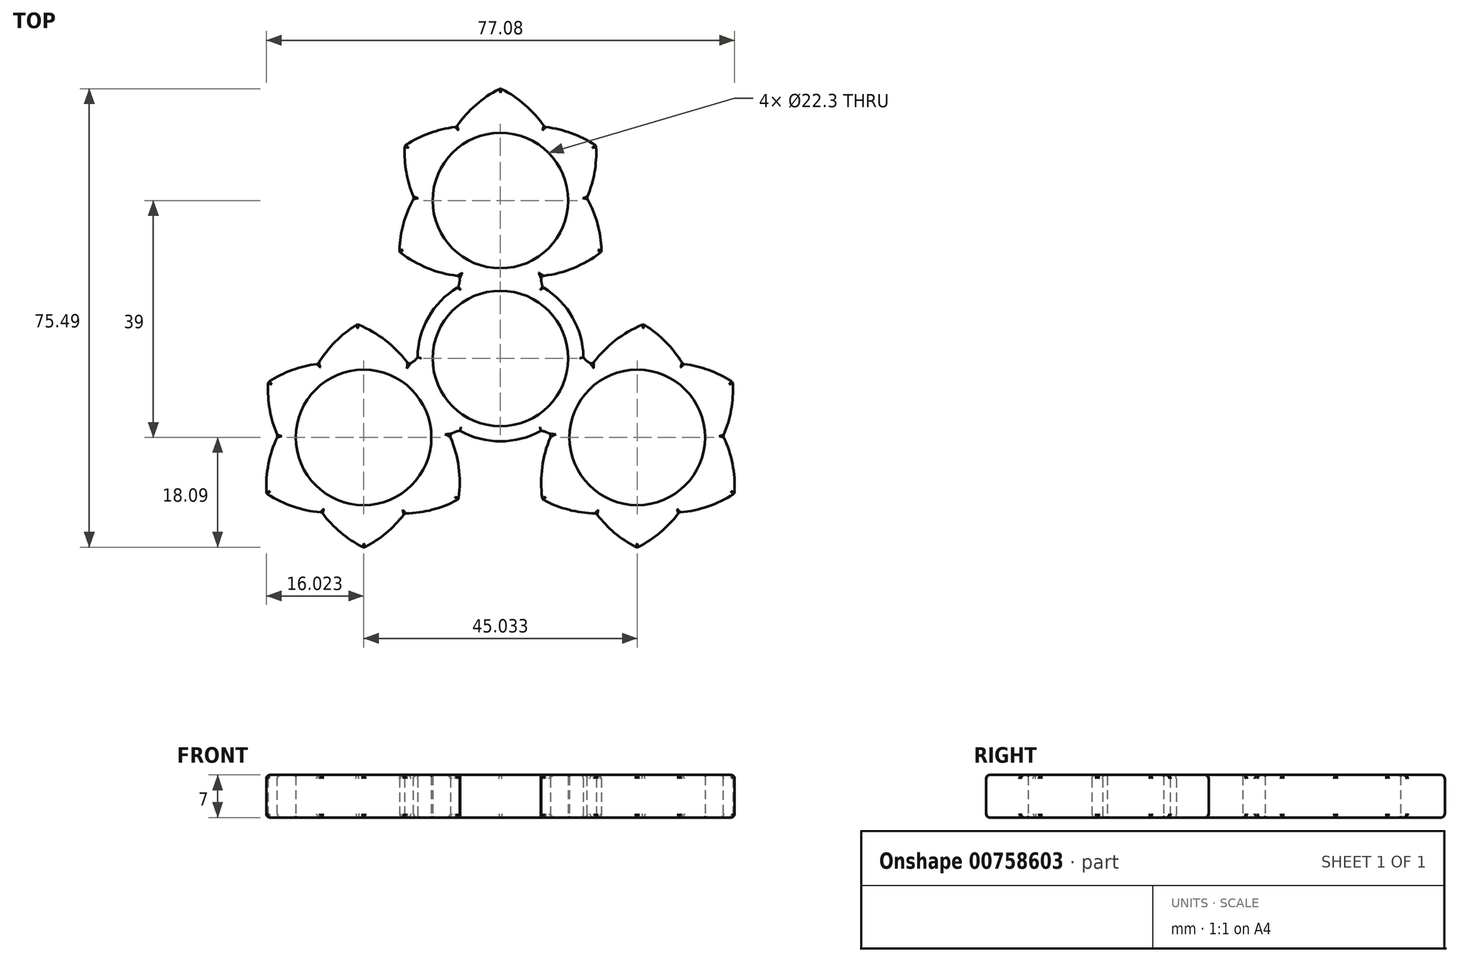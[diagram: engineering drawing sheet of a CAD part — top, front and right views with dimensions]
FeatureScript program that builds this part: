
annotation { "Feature Type Name" : "Feature", "Feature Type Description" : "" }
export const myFeature = defineFeature(function(context is Context, id is Id, definition is map)
    precondition{}
    {
        {
            var Q0;
            Q0=qCreatedBy(makeId("Top.planeOp"),FACE);
            var sketch = newSketch(context, id + "F0", { "sketchPlane" : qUnion([Q0])});
            skCircle(sketch, "E0", {"center": v(0, 0) * mm, "radius": 11.15 * mm});
            skArc(sketch, "E1.0", {"start": v(-5.17, 12.63) * mm, "mid": v(-6.92, 11.76) * mm, "end": v(-8.53, 10.66) * mm, "construction": true});
            skLineSegment(sketch, "E2", {"start": v(0, 0) * mm, "end": v(0, 26) * mm, "construction": true});
            skCircle(sketch, "E3", {"center": v(0, 26) * mm, "radius": 11.15 * mm});
            skArc(sketch, "E4.0", {"start": v(7, 14.28) * mm, "mid": v(0, 39.65) * mm, "end": v(-7, 14.28) * mm});
            skPoint(sketch, "E5.visualSharp", {"position": v(0, 16.7) * mm});
            skLineSegment(sketch, "E6.0", {"start": v(7, 0) * mm, "end": v(7, 29.5) * mm, "construction": true});
            skArc(sketch, "E7.trimOffspring", {"start": v(-7, 11.72) * mm, "mid": v(0, -13.65) * mm, "end": v(7, 11.72) * mm});
            skArc(sketch, "E8", {"start": v(7, 14.28) * mm, "mid": v(6.7, 13) * mm, "end": v(7, 11.72) * mm});
            skArc(sketch, "E9.MirrorCS", {"start": v(-7, 14.28) * mm, "mid": v(-6.7, 13) * mm, "end": v(-7, 11.72) * mm});
            skArc(sketch, "E10", {"start": v(0, 44.46) * mm, "mid": v(-4.47, 41.37) * mm, "end": v(-7.9, 37.13) * mm});
            skArc(sketch, "E11.MirrorCS", {"start": v(0, 44.46) * mm, "mid": v(4.47, 41.37) * mm, "end": v(7.9, 37.13) * mm});
            skArc(sketch, "E12", {"start": v(16.64, 17.58) * mm, "mid": v(15.74, 22.94) * mm, "end": v(13.37, 27.84) * mm});
            skArc(sketch, "E13.MirrorCS", {"start": v(16.64, 17.58) * mm, "mid": v(11.93, 14.85) * mm, "end": v(6.64, 13.55) * mm});
            skArc(sketch, "E14.MirrorCS", {"start": v(-15.74, 35.04) * mm, "mid": v(-15.27, 29.62) * mm, "end": v(-13.3, 24.55) * mm});
            skArc(sketch, "E15.MirrorCS", {"start": v(-15.74, 35.04) * mm, "mid": v(-10.82, 37.39) * mm, "end": v(-5.45, 38.25) * mm});
            skArc(sketch, "E16.MirrorCS", {"start": v(15.74, 35.04) * mm, "mid": v(10.82, 37.39) * mm, "end": v(5.45, 38.25) * mm});
            skArc(sketch, "E17.MirrorCS", {"start": v(15.74, 35.04) * mm, "mid": v(15.27, 29.62) * mm, "end": v(13.3, 24.55) * mm});
            skArc(sketch, "E18.MirrorCS", {"start": v(-16.64, 17.58) * mm, "mid": v(-15.74, 22.94) * mm, "end": v(-13.37, 27.84) * mm});
            skArc(sketch, "E19.MirrorCS", {"start": v(-16.64, 17.58) * mm, "mid": v(-11.93, 14.85) * mm, "end": v(-6.64, 13.55) * mm});
            skSolve(sketch);
        }
        {
            var Q0;
            Q0=qSketchRegion(id+"F2",true);
            var Q1;
            Q1=qSketchRegion(id+"F0",true);
            var Q2;
            {var subQ0=sQuery(id+"F0.wireOp",EDGE,"5286eaf0-ed28-4451-94e3-1d908ec19ca7");var subQ1=sQuery(id+"F0.wireOp",EDGE,"E3");var subQ2=makeQuery(id+"F0.imprint","INTERSECT",VERTEX,{"disambiguationData":[OD(0.0)],"derivedFrom":[subQ1,subQ0]});Q2=makeQuery(id+"F0.imprint","IMPRINT",FACE,{"disambiguationData":[TD([[makeQuery(id+"F0.imprint","IMPRINT",EDGE,{"disambiguationData":[TD([[subQ2,-1.0]])],"derivedFrom":subQ1}),-1.0]])]});}
            var Q3;
            {var subQ0=sQuery(id+"F0.wireOp",EDGE,"972e2314-292c-46cc-950a-d2e98ffed2b1");var subQ1=sQuery(id+"F0.wireOp",EDGE,"E3");var subQ2=makeQuery(id+"F0.imprint","INTERSECT",VERTEX,{"disambiguationData":[OD(0.0)],"derivedFrom":[subQ1,subQ0]});Q3=makeQuery(id+"F0.imprint","IMPRINT",FACE,{"disambiguationData":[TD([[makeQuery(id+"F0.imprint","IMPRINT",EDGE,{"disambiguationData":[TD([[subQ2,-1.0]])],"derivedFrom":subQ1}),-1.0]])]});}
            var Q4;
            {var subQ0=sQuery(id+"F0.wireOp",EDGE,"8576df35-fd95-4b7d-8476-f7b5d8a5ebd1");var subQ1=sQuery(id+"F0.wireOp",EDGE,"E3");var subQ2=makeQuery(id+"F0.imprint","INTERSECT",VERTEX,{"disambiguationData":[OD(0.0)],"derivedFrom":[subQ1,subQ0]});Q4=makeQuery(id+"F0.imprint","IMPRINT",FACE,{"disambiguationData":[TD([[makeQuery(id+"F0.imprint","IMPRINT",EDGE,{"disambiguationData":[TD([[subQ2,-1.0]])],"derivedFrom":subQ1}),-1.0]])]});}
            var Q5;
            {var subQ0=sQuery(id+"F0.wireOp",EDGE,"upsWoKqN-qIG4-cDSa-tKJD-hM69GbnP515O");var subQ1=sQuery(id+"F0.wireOp",EDGE,"E3");var subQ2=makeQuery(id+"F0.imprint","INTERSECT",VERTEX,{"disambiguationData":[OD(0.0)],"derivedFrom":[subQ1,subQ0]});Q5=makeQuery(id+"F0.imprint","IMPRINT",FACE,{"disambiguationData":[TD([[makeQuery(id+"F0.imprint","IMPRINT",EDGE,{"disambiguationData":[TD([[subQ2,-1.0]])],"derivedFrom":subQ1}),-1.0]])]});}
            var Q6;
            {var subQ0=sQuery(id+"F0.wireOp",EDGE,"2dc68220-ebba-422f-adc0-bbb553f4a656");var subQ1=sQuery(id+"F0.wireOp",EDGE,"E3");var subQ2=makeQuery(id+"F0.imprint","INTERSECT",VERTEX,{"disambiguationData":[OD(0.0)],"derivedFrom":[subQ1,subQ0]});Q6=makeQuery(id+"F0.imprint","IMPRINT",FACE,{"disambiguationData":[TD([[makeQuery(id+"F0.imprint","IMPRINT",EDGE,{"disambiguationData":[TD([[subQ2,-1.0]])],"derivedFrom":subQ1}),-1.0]])]});}
            var Q7;
            {var subQ0=sQuery(id+"F0.wireOp",EDGE,"70cbc2a9-83ff-4b48-bb73-ff75b1e053e5");var subQ1=sQuery(id+"F0.wireOp",EDGE,"E3");var subQ2=makeQuery(id+"F0.imprint","INTERSECT",VERTEX,{"disambiguationData":[OD(0.0)],"derivedFrom":[subQ1,subQ0]});Q7=makeQuery(id+"F0.imprint","IMPRINT",FACE,{"disambiguationData":[TD([[makeQuery(id+"F0.imprint","IMPRINT",EDGE,{"disambiguationData":[TD([[subQ2,1.0]])],"derivedFrom":subQ1}),-1.0]])]});}
            var Q8;
            {var subQ0=sQuery(id+"F0.wireOp",EDGE,"8457dc48-e8ce-439c-b6e1-438fe0c9034f");var subQ1=sQuery(id+"F0.wireOp",EDGE,"E3");var subQ2=makeQuery(id+"F0.imprint","INTERSECT",VERTEX,{"disambiguationData":[OD(0.0)],"derivedFrom":[subQ1,subQ0]});Q8=makeQuery(id+"F0.imprint","IMPRINT",FACE,{"disambiguationData":[TD([[makeQuery(id+"F0.imprint","IMPRINT",EDGE,{"disambiguationData":[TD([[subQ2,-1.0]])],"derivedFrom":subQ1}),-1.0]])]});}
            var Q9;
            {var subQ0=sQuery(id+"F0.wireOp",EDGE,"6db5ce6a-88a4-4cba-8603-f791245f7d5f");var subQ1=sQuery(id+"F0.wireOp",EDGE,"E3");var subQ2=makeQuery(id+"F0.imprint","INTERSECT",VERTEX,{"disambiguationData":[OD(0.0)],"derivedFrom":[subQ1,subQ0]});Q9=makeQuery(id+"F0.imprint","IMPRINT",FACE,{"disambiguationData":[TD([[makeQuery(id+"F0.imprint","IMPRINT",EDGE,{"disambiguationData":[TD([[subQ2,-1.0]])],"derivedFrom":subQ1}),-1.0]])]});}
            var Q10;
            {var subQ0=sQuery(id+"F0.wireOp",EDGE,"26ba9915-316d-43ac-97a0-efcd31670470");var subQ1=sQuery(id+"F0.wireOp",EDGE,"E3");var subQ2=makeQuery(id+"F0.imprint","INTERSECT",VERTEX,{"disambiguationData":[OD(0.0)],"derivedFrom":[subQ1,subQ0]});Q10=makeQuery(id+"F0.imprint","IMPRINT",FACE,{"disambiguationData":[TD([[makeQuery(id+"F0.imprint","IMPRINT",EDGE,{"disambiguationData":[TD([[subQ2,-1.0]])],"derivedFrom":subQ1}),-1.0]])]});}
            extrude(context, id + "F1", {"entities" : qUnion([Q0, Q1, Q2, Q3, Q4, Q5, Q6, Q7, Q8, Q9, Q10]), "depth" : 7 * mm, "offsetDistance" : 25 * mm});
        }
        {
            var Q0;
            Q0=qCreatedBy(makeId("Right.planeOp"),FACE);
            var sketch = newSketch(context, id + "F2", { "sketchPlane" : qUnion([Q0])});
            skLineSegment(sketch, "E20", {"start": v(0, -11.35) * mm, "end": v(0, 14.45) * mm, "construction": true});
            skSolve(sketch);
        }
        {
            var Q0;
            Q0=makeQuery(id+"F1.opExtrude","SWEPT_FACE",FACE,{"disambiguationData":[OSD([sQuery(id+"F0.wireOp",EDGE,"E0")])]});
            var Q1;
            Q1=makeQuery(id+"F1.opExtrude","SWEPT_FACE",FACE,{"disambiguationData":[OSD([sQuery(id+"F0.wireOp",EDGE,"E3")])]});
            fillet(context, id + "F3", {"entities" : qUnion([Q0, Q1]), "radius" : 0.2 * mm, "tangentPropagation" : true, "allowEdgeOverflow" : false});
        }
        {
            var Q0;
            Q0=makeQuery(id+"F1.opExtrude","SWEPT_EDGE",EDGE,{"disambiguationData":[OSD([sQuery(id+"F0.wireOp",EDGE,"B6IW4b8f-rdPB-c0Us-c8Mo-Mq4TzhgtsJ4K"),sQuery(id+"F0.wireOp",EDGE,"YkMFX2vO-4Crt-TsgE-euFS-UGkuE4yFQV92")])]});
            var Q1;
            Q1=makeQuery(id+"F1.opExtrude","SWEPT_EDGE",EDGE,{"disambiguationData":[OSD([sQuery(id+"F0.wireOp",EDGE,"05Ssocvi-DhHh-OsZG-e2E6-rp3hOyrowWxE"),sQuery(id+"F0.wireOp",EDGE,"gXTc2K6m-pDrj-VkwX-DA3g-2FsoQV2dXgWA")])]});
            var Q2;
            Q2=makeQuery(id+"F1.opExtrude","SWEPT_EDGE",EDGE,{"disambiguationData":[OSD([sQuery(id+"F0.wireOp",EDGE,"WV1YJwpc-lhCt-Tkbw-pyGD-IAguLvoMxcio"),sQuery(id+"F0.wireOp",EDGE,"lRAOphcG-mkQV-B9rX-murS-RDVpryX3sv7Y")])]});
            var Q3;
            Q3=makeQuery(id+"F1.opExtrude","CAP_FACE",FACE,{"disambiguationData":[OSD([sQuery(id+"F0.wireOp",EDGE,"E0"),sQuery(id+"F0.wireOp",EDGE,"E3"),sQuery(id+"F0.wireOp",EDGE,"E4.0"),sQuery(id+"F0.wireOp",EDGE,"E7.trimOffspring"),sQuery(id+"F0.wireOp",EDGE,"E8"),sQuery(id+"F0.wireOp",EDGE,"E9.MirrorCS"),sQuery(id+"F0.wireOp",EDGE,"A4q6XAE9-nX4I-gney-ZS84-N0PxHdFMNtC2"),sQuery(id+"F0.wireOp",EDGE,"90f88150-1d21-4d5f-99c7-c443b2953583"),sQuery(id+"F0.wireOp",EDGE,"aea63897-bdd4-478d-acf8-b9e86850efd0"),sQuery(id+"F0.wireOp",EDGE,"e52c3788-5800-4ccf-9de2-e600990ce032"),sQuery(id+"F0.wireOp",EDGE,"6943e6b1-6e27-4218-960a-470c6ffbd814"),sQuery(id+"F0.wireOp",EDGE,"dd87b57e-f014-4439-b0ae-6b8a5318a583"),sQuery(id+"F0.wireOp",EDGE,"9d18db76-b666-4d6e-9b71-35c6185a29a1")])],"isStart":false});
            var Q4;
            Q4=makeQuery(id+"F1.opExtrude","CAP_FACE",FACE,{"disambiguationData":[OSD([sQuery(id+"F0.wireOp",EDGE,"E0"),sQuery(id+"F0.wireOp",EDGE,"E3"),sQuery(id+"F0.wireOp",EDGE,"E4.0"),sQuery(id+"F0.wireOp",EDGE,"E7.trimOffspring"),sQuery(id+"F0.wireOp",EDGE,"E8"),sQuery(id+"F0.wireOp",EDGE,"E9.MirrorCS"),sQuery(id+"F0.wireOp",EDGE,"A4q6XAE9-nX4I-gney-ZS84-N0PxHdFMNtC2"),sQuery(id+"F0.wireOp",EDGE,"90f88150-1d21-4d5f-99c7-c443b2953583"),sQuery(id+"F0.wireOp",EDGE,"aea63897-bdd4-478d-acf8-b9e86850efd0"),sQuery(id+"F0.wireOp",EDGE,"e52c3788-5800-4ccf-9de2-e600990ce032"),sQuery(id+"F0.wireOp",EDGE,"6943e6b1-6e27-4218-960a-470c6ffbd814"),sQuery(id+"F0.wireOp",EDGE,"dd87b57e-f014-4439-b0ae-6b8a5318a583"),sQuery(id+"F0.wireOp",EDGE,"9d18db76-b666-4d6e-9b71-35c6185a29a1")])],"isStart":true});
            fillet(context, id + "F4", {"entities" : qUnion([Q0, Q1, Q2, Q3, Q4]), "radius" : 0.6 * mm, "tangentPropagation" : true, "allowEdgeOverflow" : false});
        }
        {
            var Q0;
            Q0=makeQuery(id+"F1.opExtrude","SWEPT_BODY",BODY,{"disambiguationData":[OSD([sQuery(id+"F0.wireOp",EDGE,"E0"),sQuery(id+"F0.wireOp",EDGE,"E1.0"),sQuery(id+"F0.wireOp",EDGE,"E3"),sQuery(id+"F0.wireOp",EDGE,"E4.0"),sQuery(id+"F0.wireOp",EDGE,"7c884c8c-e37f-41f7-9a8e-9150e4511ce8.0"),sQuery(id+"F0.wireOp",EDGE,"124d70be-8a2f-4ff1-8067-023c3a760d13.0"),sQuery(id+"F0.wireOp",EDGE,"7qioyo7K-iHsX-Xa6s-X97m-BwtuQXfGrCvp"),sQuery(id+"F0.wireOp",EDGE,"oFAU7C9Q-nsB6-dseo-MMuZ-7hNLlDQCrwbt"),sQuery(id+"F0.wireOp",EDGE,"a2486781-22df-47b1-8026-fe576fbc433f.0"),sQuery(id+"F0.wireOp",EDGE,"cb9c9ce2-17e4-408e-8bf5-b38f411324f0.0"),sQuery(id+"F0.wireOp",EDGE,"jKmUo85i-UXFQ-YKQP-mafa-QPdGbBQ2pSZu"),sQuery(id+"F0.wireOp",EDGE,"14rnQz0T-OoW9-SuH9-BmvN-4Fd0IeYT7QfG")])]});
            var Q1;
            Q1=sQuery(id+"F2.wireOp",EDGE,"E20");
            circularPattern(context, id + "F5", {"operationType" : NewBodyOperationType.ADD, "entities" : qUnion([Q0]), "axis" : qUnion([Q1]), "angle" : 360 * degree, "instanceCount" : 3, "equalSpace" : true});
        }
        {
            var Q0;
            Q0=makeQuery(id+"F5.opPattern","COPY",EDGE,{"derivedFrom":makeQuery(id+"F1.opExtrude","SWEPT_EDGE",EDGE,{"disambiguationData":[OSD([sQuery(id+"F0.wireOp",EDGE,"E14.MirrorCS"),sQuery(id+"F0.wireOp",EDGE,"E15.MirrorCS")])]}),"instanceName":"1"});
            var Q1;
            Q1=makeQuery(id+"F5.opPattern","COPY",EDGE,{"derivedFrom":makeQuery(id+"F1.opExtrude","SWEPT_EDGE",EDGE,{"disambiguationData":[OSD([sQuery(id+"F0.wireOp",EDGE,"E18.MirrorCS"),sQuery(id+"F0.wireOp",EDGE,"E19.MirrorCS")])]}),"instanceName":"1"});
            var Q2;
            Q2=makeQuery(id+"F5.opPattern","COPY",EDGE,{"derivedFrom":makeQuery(id+"F1.opExtrude","SWEPT_EDGE",EDGE,{"disambiguationData":[OSD([sQuery(id+"F0.wireOp",EDGE,"E10"),sQuery(id+"F0.wireOp",EDGE,"E11.MirrorCS")])]}),"instanceName":"1"});
            var Q3;
            Q3=makeQuery(id+"F5.opPattern","COPY",EDGE,{"derivedFrom":makeQuery(id+"F1.opExtrude","SWEPT_EDGE",EDGE,{"disambiguationData":[OSD([sQuery(id+"F0.wireOp",EDGE,"E16.MirrorCS"),sQuery(id+"F0.wireOp",EDGE,"E17.MirrorCS")])]}),"instanceName":"1"});
            var Q4;
            Q4=makeQuery(id+"F5.opPattern","COPY",EDGE,{"derivedFrom":makeQuery(id+"F1.opExtrude","SWEPT_EDGE",EDGE,{"disambiguationData":[OSD([sQuery(id+"F0.wireOp",EDGE,"E12"),sQuery(id+"F0.wireOp",EDGE,"E13.MirrorCS")])]}),"instanceName":"1"});
            var Q5;
            Q5=makeQuery(id+"F5.opPattern","COPY",EDGE,{"derivedFrom":makeQuery(id+"F1.opExtrude","SWEPT_EDGE",EDGE,{"disambiguationData":[OSD([sQuery(id+"F0.wireOp",EDGE,"E12"),sQuery(id+"F0.wireOp",EDGE,"E17.MirrorCS")])]}),"instanceName":"1"});
            var Q6;
            Q6=makeQuery(id+"F5.opPattern","COPY",EDGE,{"derivedFrom":makeQuery(id+"F1.opExtrude","SWEPT_EDGE",EDGE,{"disambiguationData":[OSD([sQuery(id+"F0.wireOp",EDGE,"E11.MirrorCS"),sQuery(id+"F0.wireOp",EDGE,"E16.MirrorCS")])]}),"instanceName":"1"});
            var Q7;
            Q7=makeQuery(id+"F5.opPattern","COPY",EDGE,{"derivedFrom":makeQuery(id+"F1.opExtrude","SWEPT_EDGE",EDGE,{"disambiguationData":[OSD([sQuery(id+"F0.wireOp",EDGE,"E10"),sQuery(id+"F0.wireOp",EDGE,"E15.MirrorCS")])]}),"instanceName":"1"});
            var Q8;
            Q8=makeQuery(id+"F5.opPattern","COPY",EDGE,{"derivedFrom":makeQuery(id+"F1.opExtrude","SWEPT_EDGE",EDGE,{"disambiguationData":[OSD([sQuery(id+"F0.wireOp",EDGE,"E14.MirrorCS"),sQuery(id+"F0.wireOp",EDGE,"E18.MirrorCS")])]}),"instanceName":"1"});
            var Q9;
            Q9=makeQuery(id+"F5.opPattern","COPY",EDGE,{"derivedFrom":makeQuery(id+"F1.opExtrude","SWEPT_EDGE",EDGE,{"disambiguationData":[OSD([sQuery(id+"F0.wireOp",EDGE,"E9.MirrorCS"),sQuery(id+"F0.wireOp",EDGE,"E19.MirrorCS")])]}),"instanceName":"1"});
            var Q10;
            Q10=makeQuery(id+"F5.opPattern","COPY",EDGE,{"derivedFrom":makeQuery(id+"F1.opExtrude","SWEPT_EDGE",EDGE,{"disambiguationData":[OSD([sQuery(id+"F0.wireOp",EDGE,"E7.trimOffspring"),sQuery(id+"F0.wireOp",EDGE,"E9.MirrorCS")])]}),"instanceName":"1"});
            var Q11;
            Q11=makeQuery(id+"F5.opPattern","COPY",EDGE,{"derivedFrom":makeQuery(id+"F1.opExtrude","SWEPT_EDGE",EDGE,{"disambiguationData":[OSD([sQuery(id+"F0.wireOp",EDGE,"E8"),sQuery(id+"F0.wireOp",EDGE,"E13.MirrorCS")])]}),"instanceName":"1"});
            var Q12;
            Q12=makeQuery(id+"F5.opPattern","COPY",EDGE,{"derivedFrom":makeQuery(id+"F1.opExtrude","SWEPT_EDGE",EDGE,{"disambiguationData":[OSD([sQuery(id+"F0.wireOp",EDGE,"E7.trimOffspring"),sQuery(id+"F0.wireOp",EDGE,"E8")])]}),"instanceName":"1"});
            var Q13;
            Q13=makeQuery(id+"F5.opPattern","COPY",EDGE,{"derivedFrom":makeQuery(id+"F1.opExtrude","SWEPT_EDGE",EDGE,{"disambiguationData":[OSD([sQuery(id+"F0.wireOp",EDGE,"E7.trimOffspring"),sQuery(id+"F0.wireOp",EDGE,"E8")])]}),"instanceName":"2"});
            var Q14;
            Q14=makeQuery(id+"F5.opPattern","COPY",EDGE,{"derivedFrom":makeQuery(id+"F1.opExtrude","SWEPT_EDGE",EDGE,{"disambiguationData":[OSD([sQuery(id+"F0.wireOp",EDGE,"E8"),sQuery(id+"F0.wireOp",EDGE,"E13.MirrorCS")])]}),"instanceName":"2"});
            var Q15;
            Q15=makeQuery(id+"F5.opPattern","COPY",EDGE,{"derivedFrom":makeQuery(id+"F1.opExtrude","SWEPT_EDGE",EDGE,{"disambiguationData":[OSD([sQuery(id+"F0.wireOp",EDGE,"E12"),sQuery(id+"F0.wireOp",EDGE,"E13.MirrorCS")])]}),"instanceName":"2"});
            var Q16;
            Q16=makeQuery(id+"F5.opPattern","COPY",EDGE,{"derivedFrom":makeQuery(id+"F1.opExtrude","SWEPT_EDGE",EDGE,{"disambiguationData":[OSD([sQuery(id+"F0.wireOp",EDGE,"E12"),sQuery(id+"F0.wireOp",EDGE,"E17.MirrorCS")])]}),"instanceName":"2"});
            var Q17;
            Q17=makeQuery(id+"F5.opPattern","COPY",EDGE,{"derivedFrom":makeQuery(id+"F1.opExtrude","SWEPT_EDGE",EDGE,{"disambiguationData":[OSD([sQuery(id+"F0.wireOp",EDGE,"E16.MirrorCS"),sQuery(id+"F0.wireOp",EDGE,"E17.MirrorCS")])]}),"instanceName":"2"});
            var Q18;
            Q18=makeQuery(id+"F5.opPattern","COPY",EDGE,{"derivedFrom":makeQuery(id+"F1.opExtrude","SWEPT_EDGE",EDGE,{"disambiguationData":[OSD([sQuery(id+"F0.wireOp",EDGE,"E11.MirrorCS"),sQuery(id+"F0.wireOp",EDGE,"E16.MirrorCS")])]}),"instanceName":"2"});
            var Q19;
            Q19=makeQuery(id+"F5.opPattern","COPY",EDGE,{"derivedFrom":makeQuery(id+"F1.opExtrude","SWEPT_EDGE",EDGE,{"disambiguationData":[OSD([sQuery(id+"F0.wireOp",EDGE,"E10"),sQuery(id+"F0.wireOp",EDGE,"E11.MirrorCS")])]}),"instanceName":"2"});
            var Q20;
            Q20=makeQuery(id+"F5.opPattern","COPY",EDGE,{"derivedFrom":makeQuery(id+"F1.opExtrude","SWEPT_EDGE",EDGE,{"disambiguationData":[OSD([sQuery(id+"F0.wireOp",EDGE,"E10"),sQuery(id+"F0.wireOp",EDGE,"E15.MirrorCS")])]}),"instanceName":"2"});
            var Q21;
            Q21=makeQuery(id+"F5.opPattern","COPY",EDGE,{"derivedFrom":makeQuery(id+"F1.opExtrude","SWEPT_EDGE",EDGE,{"disambiguationData":[OSD([sQuery(id+"F0.wireOp",EDGE,"E14.MirrorCS"),sQuery(id+"F0.wireOp",EDGE,"E15.MirrorCS")])]}),"instanceName":"2"});
            var Q22;
            Q22=makeQuery(id+"F5.opPattern","COPY",EDGE,{"derivedFrom":makeQuery(id+"F1.opExtrude","SWEPT_EDGE",EDGE,{"disambiguationData":[OSD([sQuery(id+"F0.wireOp",EDGE,"E14.MirrorCS"),sQuery(id+"F0.wireOp",EDGE,"E18.MirrorCS")])]}),"instanceName":"2"});
            var Q23;
            Q23=makeQuery(id+"F5.opPattern","COPY",EDGE,{"derivedFrom":makeQuery(id+"F1.opExtrude","SWEPT_EDGE",EDGE,{"disambiguationData":[OSD([sQuery(id+"F0.wireOp",EDGE,"E18.MirrorCS"),sQuery(id+"F0.wireOp",EDGE,"E19.MirrorCS")])]}),"instanceName":"2"});
            var Q24;
            Q24=makeQuery(id+"F5.opPattern","COPY",EDGE,{"derivedFrom":makeQuery(id+"F1.opExtrude","SWEPT_EDGE",EDGE,{"disambiguationData":[OSD([sQuery(id+"F0.wireOp",EDGE,"E9.MirrorCS"),sQuery(id+"F0.wireOp",EDGE,"E19.MirrorCS")])]}),"instanceName":"2"});
            var Q25;
            Q25=makeQuery(id+"F5.opPattern","COPY",EDGE,{"derivedFrom":makeQuery(id+"F1.opExtrude","SWEPT_EDGE",EDGE,{"disambiguationData":[OSD([sQuery(id+"F0.wireOp",EDGE,"E7.trimOffspring"),sQuery(id+"F0.wireOp",EDGE,"E9.MirrorCS")])]}),"instanceName":"2"});
            var Q26;
            Q26=makeQuery(id+"F1.opExtrude","SWEPT_EDGE",EDGE,{"disambiguationData":[OSD([sQuery(id+"F0.wireOp",EDGE,"E7.trimOffspring"),sQuery(id+"F0.wireOp",EDGE,"E8")])]});
            var Q27;
            Q27=makeQuery(id+"F1.opExtrude","SWEPT_EDGE",EDGE,{"disambiguationData":[OSD([sQuery(id+"F0.wireOp",EDGE,"E8"),sQuery(id+"F0.wireOp",EDGE,"E13.MirrorCS")])]});
            var Q28;
            Q28=makeQuery(id+"F1.opExtrude","SWEPT_EDGE",EDGE,{"disambiguationData":[OSD([sQuery(id+"F0.wireOp",EDGE,"E12"),sQuery(id+"F0.wireOp",EDGE,"E13.MirrorCS")])]});
            var Q29;
            Q29=makeQuery(id+"F1.opExtrude","SWEPT_EDGE",EDGE,{"disambiguationData":[OSD([sQuery(id+"F0.wireOp",EDGE,"E12"),sQuery(id+"F0.wireOp",EDGE,"E17.MirrorCS")])]});
            var Q30;
            Q30=makeQuery(id+"F1.opExtrude","SWEPT_EDGE",EDGE,{"disambiguationData":[OSD([sQuery(id+"F0.wireOp",EDGE,"E16.MirrorCS"),sQuery(id+"F0.wireOp",EDGE,"E17.MirrorCS")])]});
            var Q31;
            Q31=makeQuery(id+"F1.opExtrude","SWEPT_EDGE",EDGE,{"disambiguationData":[OSD([sQuery(id+"F0.wireOp",EDGE,"E11.MirrorCS"),sQuery(id+"F0.wireOp",EDGE,"E16.MirrorCS")])]});
            var Q32;
            Q32=makeQuery(id+"F1.opExtrude","SWEPT_EDGE",EDGE,{"disambiguationData":[OSD([sQuery(id+"F0.wireOp",EDGE,"E10"),sQuery(id+"F0.wireOp",EDGE,"E11.MirrorCS")])]});
            var Q33;
            Q33=makeQuery(id+"F1.opExtrude","SWEPT_EDGE",EDGE,{"disambiguationData":[OSD([sQuery(id+"F0.wireOp",EDGE,"E10"),sQuery(id+"F0.wireOp",EDGE,"E15.MirrorCS")])]});
            var Q34;
            Q34=makeQuery(id+"F1.opExtrude","SWEPT_EDGE",EDGE,{"disambiguationData":[OSD([sQuery(id+"F0.wireOp",EDGE,"E14.MirrorCS"),sQuery(id+"F0.wireOp",EDGE,"E15.MirrorCS")])]});
            var Q35;
            Q35=makeQuery(id+"F1.opExtrude","SWEPT_EDGE",EDGE,{"disambiguationData":[OSD([sQuery(id+"F0.wireOp",EDGE,"E14.MirrorCS"),sQuery(id+"F0.wireOp",EDGE,"E18.MirrorCS")])]});
            var Q36;
            Q36=makeQuery(id+"F1.opExtrude","SWEPT_EDGE",EDGE,{"disambiguationData":[OSD([sQuery(id+"F0.wireOp",EDGE,"E18.MirrorCS"),sQuery(id+"F0.wireOp",EDGE,"E19.MirrorCS")])]});
            var Q37;
            Q37=makeQuery(id+"F1.opExtrude","SWEPT_EDGE",EDGE,{"disambiguationData":[OSD([sQuery(id+"F0.wireOp",EDGE,"E9.MirrorCS"),sQuery(id+"F0.wireOp",EDGE,"E19.MirrorCS")])]});
            var Q38;
            Q38=makeQuery(id+"F1.opExtrude","SWEPT_EDGE",EDGE,{"disambiguationData":[OSD([sQuery(id+"F0.wireOp",EDGE,"E7.trimOffspring"),sQuery(id+"F0.wireOp",EDGE,"E9.MirrorCS")])]});
            fillet(context, id + "F6", {"entities" : qUnion([Q0, Q1, Q2, Q3, Q4, Q5, Q6, Q7, Q8, Q9, Q10, Q11, Q12, Q13, Q14, Q15, Q16, Q17, Q18, Q19, Q20, Q21, Q22, Q23, Q24, Q25, Q26, Q27, Q28, Q29, Q30, Q31, Q32, Q33, Q34, Q35, Q36, Q37, Q38]), "radius" : .5 * mm, "tangentPropagation" : true, "allowEdgeOverflow" : false});
        }
    });
